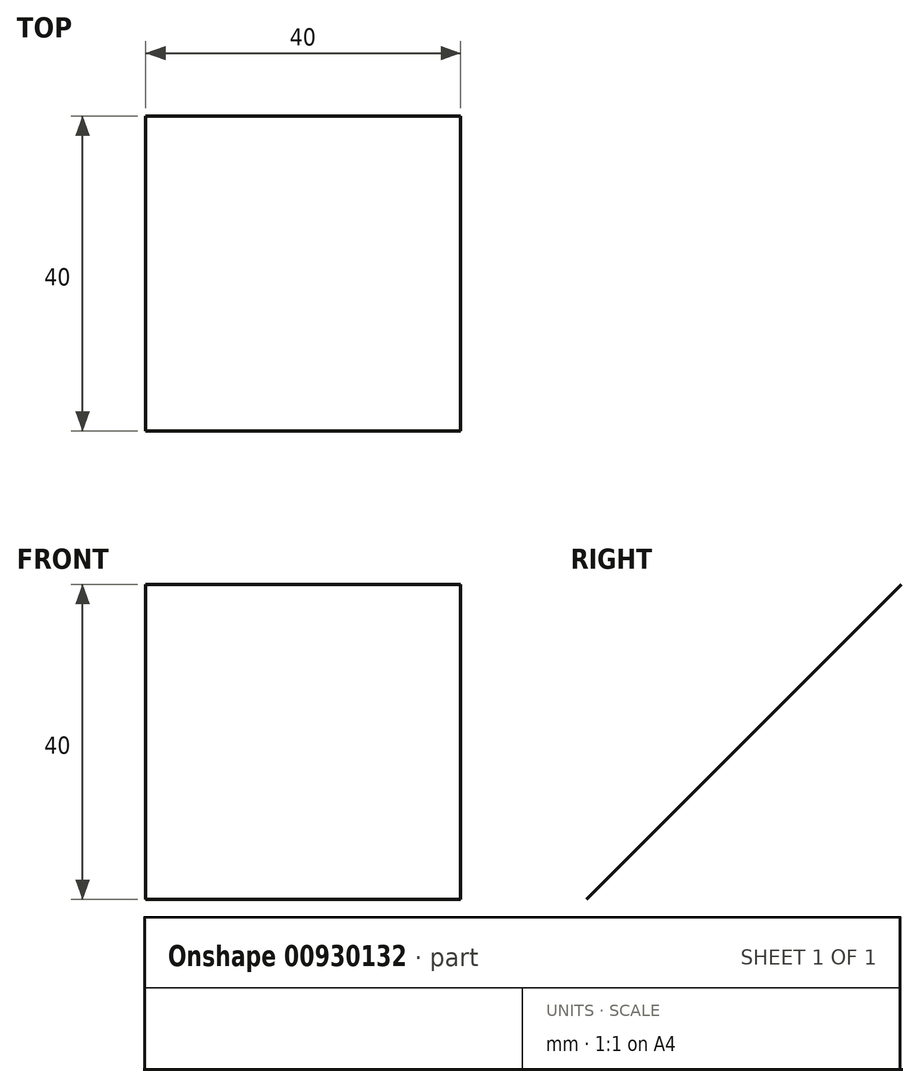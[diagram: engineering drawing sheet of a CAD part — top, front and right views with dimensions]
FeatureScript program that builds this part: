
annotation { "Feature Type Name" : "Feature", "Feature Type Description" : "" }
export const myFeature = defineFeature(function(context is Context, id is Id, definition is map)
    precondition{}
    {
        {
            var Q0;
            Q0=qCreatedBy(makeId("Front.planeOp"),FACE);
            var sketch = newSketch(context, id + "F0", { "sketchPlane" : qUnion([Q0])});
            skLineSegment(sketch, "E0.bottom", {"start": v(-4.75, -8.32) * mm, "end": v(4.75, -8.32) * mm});
            skLineSegment(sketch, "E0.top", {"start": v(-4.75, 8.32) * mm, "end": v(4.75, 8.32) * mm});
            skLineSegment(sketch, "E0.left", {"start": v(-4.75, -8.32) * mm, "end": v(-4.75, 8.32) * mm});
            skLineSegment(sketch, "E0.right", {"start": v(4.75, -8.32) * mm, "end": v(4.75, 8.32) * mm});
            skSolve(sketch);
        }
        {
            var Q0;
            Q0=qCreatedBy(makeId("Right.planeOp"),FACE);
            var sketch = newSketch(context, id + "F1", { "sketchPlane" : qUnion([Q0])});
            skLineSegment(sketch, "E1", {"start": v(10.02, -20) * mm, "end": v(50.02, 20) * mm});
            skLineSegment(sketch, "E2", {"start": v(0, 0) * mm, "end": v(30.02, 0) * mm, "construction": true});
            skLineSegment(sketch, "E3", {"start": v(30.02, 0) * mm, "end": v(30.02, 27.4) * mm, "construction": true});
            skSolve(sketch);
        }
        {
            var Q0;
            Q0=sQuery(id+"F1.wireOp",EDGE,"E1");
            extrude(context, id + "F2", {"bodyType" : ToolBodyType.SURFACE, "surfaceEntities" : qUnion([Q0]), "endBound" : BoundingType.SYMMETRIC, "depth" : 40 * mm, "offsetDistance" : 25 * mm});
        }
    });
